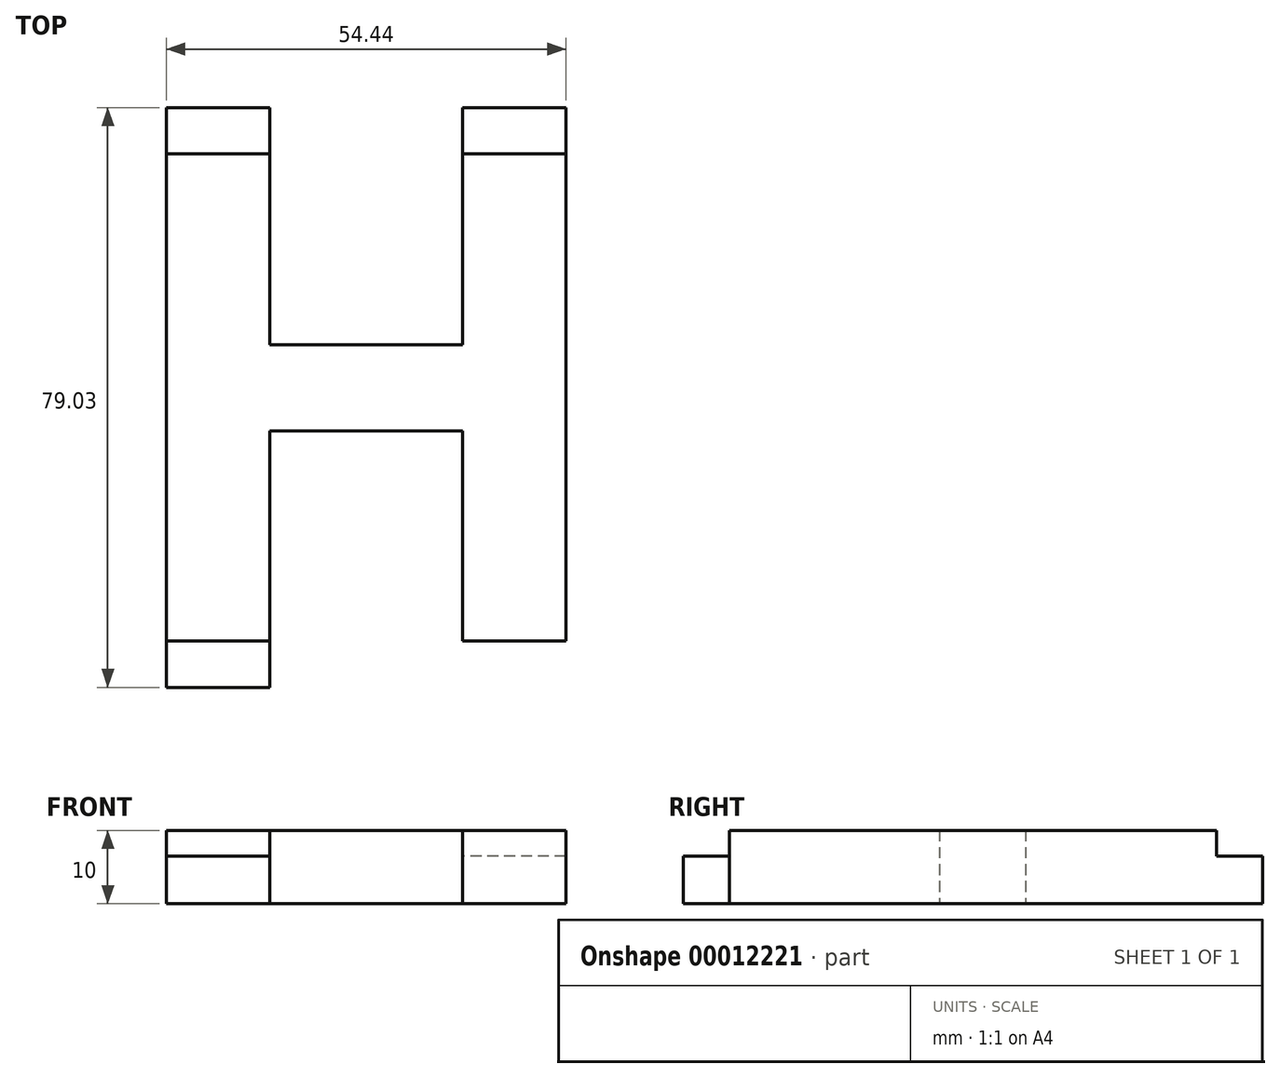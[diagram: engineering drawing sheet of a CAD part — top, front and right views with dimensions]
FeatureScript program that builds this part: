
annotation { "Feature Type Name" : "Feature", "Feature Type Description" : "" }
export const myFeature = defineFeature(function(context is Context, id is Id, definition is map)
    precondition{}
    {
        {
            var Q0;
            Q0=qCreatedBy(makeId("Top.planeOp"),FACE);
            var sketch = newSketch(context, id + "F0", { "sketchPlane" : qUnion([Q0])});
            skText(sketch, "E0", { "text": "H", "fontName": "OpenSans-Bold.ttf"});
            const initialGuessF0  = {"E0": [-0.0628, 0, 1, 0, 0.067]};
            skSetInitialGuess(sketch, initialGuessF0);
            skSolve(sketch);
        }
        {
            var Q0;
            Q0=makeQuery(id+"F0.imprint","IMPRINT",FACE,{"disambiguationData":[TD([[makeQuery(id+"F0.imprint","IMPRINT",EDGE,{"derivedFrom":sQuery(id+"F0.wireOp",EDGE,"E0.sketch_text.stroke-0")}),-1.0]])]});
            extrude(context, id + "F1", {"entities" : qUnion([Q0]), "depth" : 10 * mm});
        }
        {
            var Q0;
            Q0=makeQuery(id+"F1.opExtrude","SWEPT_FACE",FACE,{"disambiguationData":[OSD([sQuery(id+"F0.wireOp",EDGE,"E0.sketch_text.stroke-4")])]});
            var sketch = newSketch(context, id + "F2", { "sketchPlane" : qUnion([Q0])});
            skLineSegment(sketch, "E1.0.0", {"start": v(-54.44, 0) * mm, "end": v(-40.35, 0) * mm});
            skLineSegment(sketch, "E1.0.1", {"start": v(-40.35, 0) * mm, "end": v(-40.35, 10) * mm});
            skLineSegment(sketch, "E1.0.2", {"start": v(-40.35, 10) * mm, "end": v(-54.44, 10) * mm});
            skLineSegment(sketch, "E1.0.3", {"start": v(-54.44, 10) * mm, "end": v(-54.44, 0) * mm});
            skLineSegment(sketch, "E2.top", {"start": v(-54.44, 6.5) * mm, "end": v(-40.35, 6.5) * mm});
            skLineSegment(sketch, "E2.left", {"start": v(-54.44, 0) * mm, "end": v(-54.44, 6.5) * mm});
            skLineSegment(sketch, "E2.right", {"start": v(-40.35, 0) * mm, "end": v(-40.35, 6.5) * mm});
            skLineSegment(sketch, "E3.0.0", {"start": v(-14.05, 0) * mm, "end": v(0, 0) * mm});
            skLineSegment(sketch, "E3.0.1", {"start": v(0, 0) * mm, "end": v(0, 10) * mm});
            skLineSegment(sketch, "E3.0.2", {"start": v(0, 10) * mm, "end": v(-14.05, 10) * mm});
            skLineSegment(sketch, "E3.0.3", {"start": v(-14.05, 10) * mm, "end": v(-14.05, 0) * mm});
            skLineSegment(sketch, "E4.bottom", {"start": v(0, 0) * mm, "end": v(-14.05, 0) * mm});
            skLineSegment(sketch, "E4.top", {"start": v(0, 6.5) * mm, "end": v(-14.05, 6.5) * mm});
            skLineSegment(sketch, "E4.left", {"start": v(0, 0) * mm, "end": v(0, 6.5) * mm});
            skLineSegment(sketch, "E4.right", {"start": v(-14.05, 0) * mm, "end": v(-14.05, 6.5) * mm});
            skSolve(sketch);
        }
        {
            var Q0;
            Q0=makeQuery(id+"F2.imprint","IMPRINT",FACE,{"disambiguationData":[TD([[makeQuery(id+"F2.imprint","IMPRINT",EDGE,{"derivedFrom":sQuery(id+"F2.wireOp",EDGE,"E1.0.0")}),-1.0]])]});
            var Q1;
            Q1=makeQuery(id+"F2.imprint","IMPRINT",FACE,{"disambiguationData":[TD([[makeQuery(id+"F2.imprint","IMPRINT",EDGE,{"derivedFrom":sQuery(id+"F2.wireOp",EDGE,"E4.bottom")}),-1.0]])]});
            extrude(context, id + "F3", {"entities" : qUnion([Q0, Q1]), "operationType" : NewBodyOperationType.ADD, "depth" : 6.3 * mm});
        }
        {
            var Q0;
            Q0=makeQuery(id+"F1.opExtrude","SWEPT_FACE",FACE,{"disambiguationData":[OSD([sQuery(id+"F0.wireOp",EDGE,"E0.sketch_text.stroke-10")])]});
            var sketch = newSketch(context, id + "F4", { "sketchPlane" : qUnion([Q0])});
            skLineSegment(sketch, "E5.0.0", {"start": v(0, 0) * mm, "end": v(14.05, 0) * mm});
            skLineSegment(sketch, "E5.0.1", {"start": v(14.05, 0) * mm, "end": v(14.05, 10) * mm});
            skLineSegment(sketch, "E5.0.2", {"start": v(14.05, 10) * mm, "end": v(0, 10) * mm});
            skLineSegment(sketch, "E5.0.3", {"start": v(0, 10) * mm, "end": v(0, 0) * mm});
            skLineSegment(sketch, "E6.top", {"start": v(0, 6.5) * mm, "end": v(14.05, 6.5) * mm});
            skLineSegment(sketch, "E6.left", {"start": v(0, 0) * mm, "end": v(0, 6.5) * mm});
            skLineSegment(sketch, "E6.right", {"start": v(14.05, 0) * mm, "end": v(14.05, 6.5) * mm});
            skLineSegment(sketch, "E7.0.0", {"start": v(40.35, 0) * mm, "end": v(54.44, 0) * mm});
            skLineSegment(sketch, "E7.0.1", {"start": v(54.44, 0) * mm, "end": v(54.44, 10) * mm});
            skLineSegment(sketch, "E7.0.2", {"start": v(54.44, 10) * mm, "end": v(40.35, 10) * mm});
            skLineSegment(sketch, "E7.0.3", {"start": v(40.35, 10) * mm, "end": v(40.35, 0) * mm});
            skLineSegment(sketch, "E8.top", {"start": v(40.35, 6.5) * mm, "end": v(54.44, 6.5) * mm});
            skLineSegment(sketch, "E8.left", {"start": v(40.35, 0) * mm, "end": v(40.35, 6.5) * mm});
            skLineSegment(sketch, "E8.right", {"start": v(54.44, 0) * mm, "end": v(54.44, 6.5) * mm});
            skSolve(sketch);
        }
        {
            var Q0;
            Q0=makeQuery(id+"F4.imprint","IMPRINT",FACE,{"disambiguationData":[TD([[makeQuery(id+"F4.imprint","IMPRINT",EDGE,{"derivedFrom":sQuery(id+"F4.wireOp",EDGE,"E5.0.0")}),-1.0]])]});
            var Q1;
            Q1=makeQuery(id+"F4.imprint","IMPRINT",FACE,{"disambiguationData":[TD([[makeQuery(id+"F4.imprint","IMPRINT",EDGE,{"derivedFrom":sQuery(id+"F4.wireOp",EDGE,"E7.0.0")}),1.0]])]});
            extrude(context, id + "F5", {"entities" : qUnion([Q0, Q1]), "operationType" : NewBodyOperationType.ADD, "depth" : 6.3 * mm});
        }
    });
